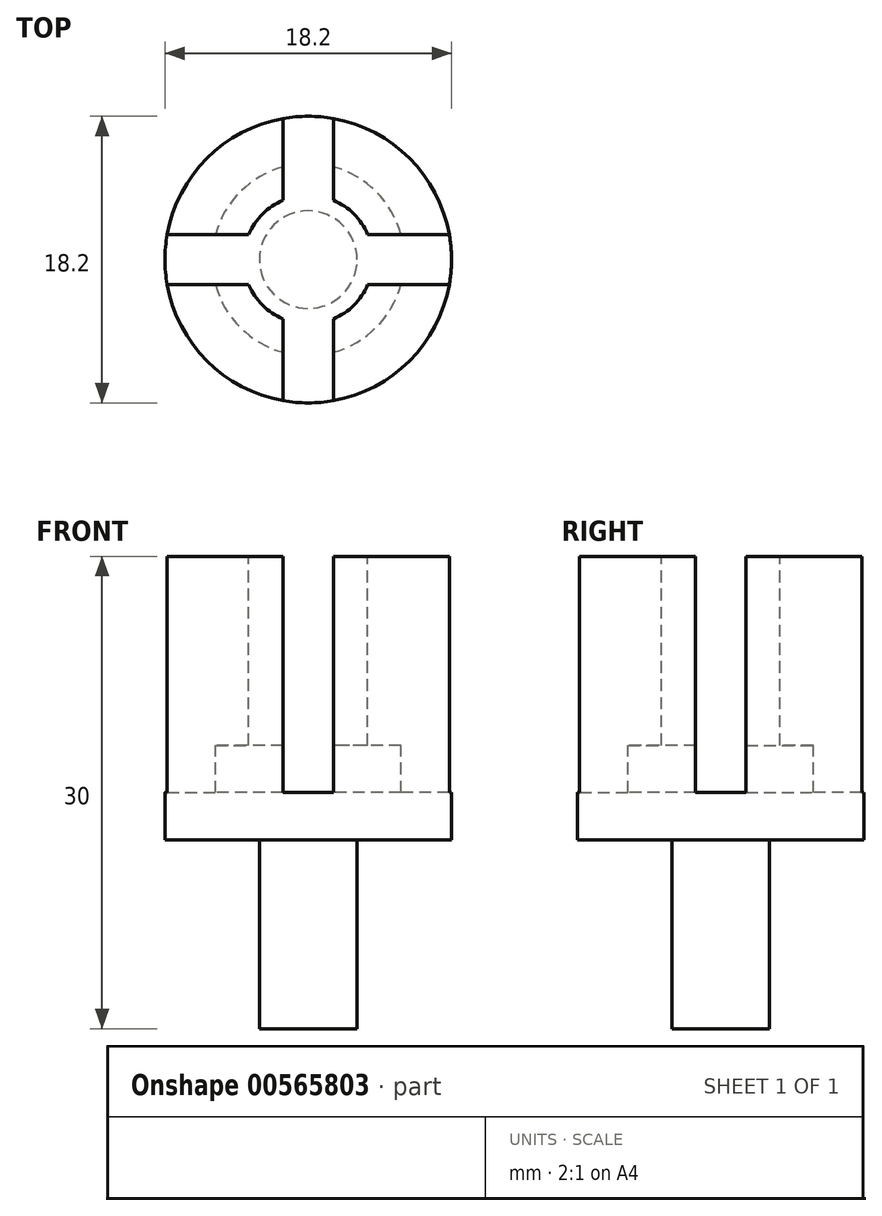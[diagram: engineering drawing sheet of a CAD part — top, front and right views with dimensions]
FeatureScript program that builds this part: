
annotation { "Feature Type Name" : "Feature", "Feature Type Description" : "" }
export const myFeature = defineFeature(function(context is Context, id is Id, definition is map)
    precondition{}
    {
        {
            var Q0;
            Q0=qCreatedBy(makeId("Front.planeOp"),FACE);
            var sketch = newSketch(context, id + "F0", { "sketchPlane" : qUnion([Q0])});
            skLineSegment(sketch, "E0", {"start": v(0, 0) * mm, "end": v(-3.1, 0) * mm});
            skLineSegment(sketch, "E1", {"start": v(-3.1, 0) * mm, "end": v(-3.1, 12) * mm});
            skLineSegment(sketch, "E2", {"start": v(-3.1, 12) * mm, "end": v(-9.1, 12) * mm});
            skLineSegment(sketch, "E3", {"start": v(-9.1, 12) * mm, "end": v(-9.1, 30) * mm});
            skLineSegment(sketch, "E4", {"start": v(-9.1, 30) * mm, "end": v(-4.1, 30) * mm});
            skLineSegment(sketch, "E5", {"start": v(0, 15) * mm, "end": v(0, 0) * mm});
            skLineSegment(sketch, "E6", {"start": v(-4.1, 30) * mm, "end": v(-4.1, 18) * mm});
            skLineSegment(sketch, "E7", {"start": v(-4.1, 18) * mm, "end": v(-6.1, 18) * mm});
            skLineSegment(sketch, "E8", {"start": v(-6.1, 18) * mm, "end": v(-6.1, 15) * mm});
            skLineSegment(sketch, "E9", {"start": v(-6.1, 15) * mm, "end": v(0, 15) * mm});
            skSolve(sketch);
        }
        {
            var Q0;
            Q0 = qSketchRegion(id + "F0", true);
            var Q1;
            Q1=sQuery(id+"F0.wireOp",EDGE,"E5");
            revolve(context, id + "F1", {"entities" : qUnion([Q0]), "axis" : qUnion([Q1]), "revolveType" : RevolveType.FULL});
        }
        {
            var Q0;
            Q0=makeQuery(id+"F1.opRevolve","SWEPT_FACE",FACE,{"disambiguationData":[OSD([sQuery(id+"F0.wireOp",EDGE,"E4")])]});
            var sketch = newSketch(context, id + "F2", { "sketchPlane" : qUnion([Q0])});
            skLineSegment(sketch, "E10", {"start": v(-1.6, 10.17) * mm, "end": v(-1.6, 3.17) * mm});
            skLineSegment(sketch, "E11", {"start": v(1.6, 10.17) * mm, "end": v(1.6, 3.17) * mm});
            skLineSegment(sketch, "E12", {"start": v(-1.6, 10.17) * mm, "end": v(1.6, 10.17) * mm});
            skLineSegment(sketch, "E13", {"start": v(-1.6, 3.17) * mm, "end": v(1.6, 3.17) * mm});
            skLineSegment(sketch, "E14.1.0", {"start": v(-10.17, -1.6) * mm, "end": v(-10.17, 1.6) * mm});
            skLineSegment(sketch, "E14.1.1", {"start": v(-10.17, -1.6) * mm, "end": v(-3.17, -1.6) * mm});
            skLineSegment(sketch, "E14.1.2", {"start": v(-10.17, 1.6) * mm, "end": v(-3.17, 1.6) * mm});
            skLineSegment(sketch, "E14.1.3", {"start": v(-3.17, -1.6) * mm, "end": v(-3.17, 1.6) * mm});
            skLineSegment(sketch, "E14.2.0", {"start": v(1.6, -10.17) * mm, "end": v(-1.6, -10.17) * mm});
            skLineSegment(sketch, "E14.2.1", {"start": v(1.6, -10.17) * mm, "end": v(1.6, -3.17) * mm});
            skLineSegment(sketch, "E14.2.2", {"start": v(-1.6, -10.17) * mm, "end": v(-1.6, -3.17) * mm});
            skLineSegment(sketch, "E14.2.3", {"start": v(1.6, -3.17) * mm, "end": v(-1.6, -3.17) * mm});
            skLineSegment(sketch, "E14.3.0", {"start": v(10.17, 1.6) * mm, "end": v(10.17, -1.6) * mm});
            skLineSegment(sketch, "E14.3.1", {"start": v(10.17, 1.6) * mm, "end": v(3.17, 1.6) * mm});
            skLineSegment(sketch, "E14.3.2", {"start": v(10.17, -1.6) * mm, "end": v(3.17, -1.6) * mm});
            skLineSegment(sketch, "E14.3.3", {"start": v(3.17, 1.6) * mm, "end": v(3.17, -1.6) * mm});
            skPoint(sketch, "E14.center", {"position": v(0, 0) * mm});
            skSolve(sketch);
        }
        {
            var Q0;
            Q0 = qSketchRegion(id + "F2", true);
            extrude(context, id + "F3", {"entities" : qUnion([Q0]), "operationType" : NewBodyOperationType.REMOVE, "oppositeDirection" : true, "depth" : 15 * mm, "offsetDistance" : 25 * mm});
        }
    });
